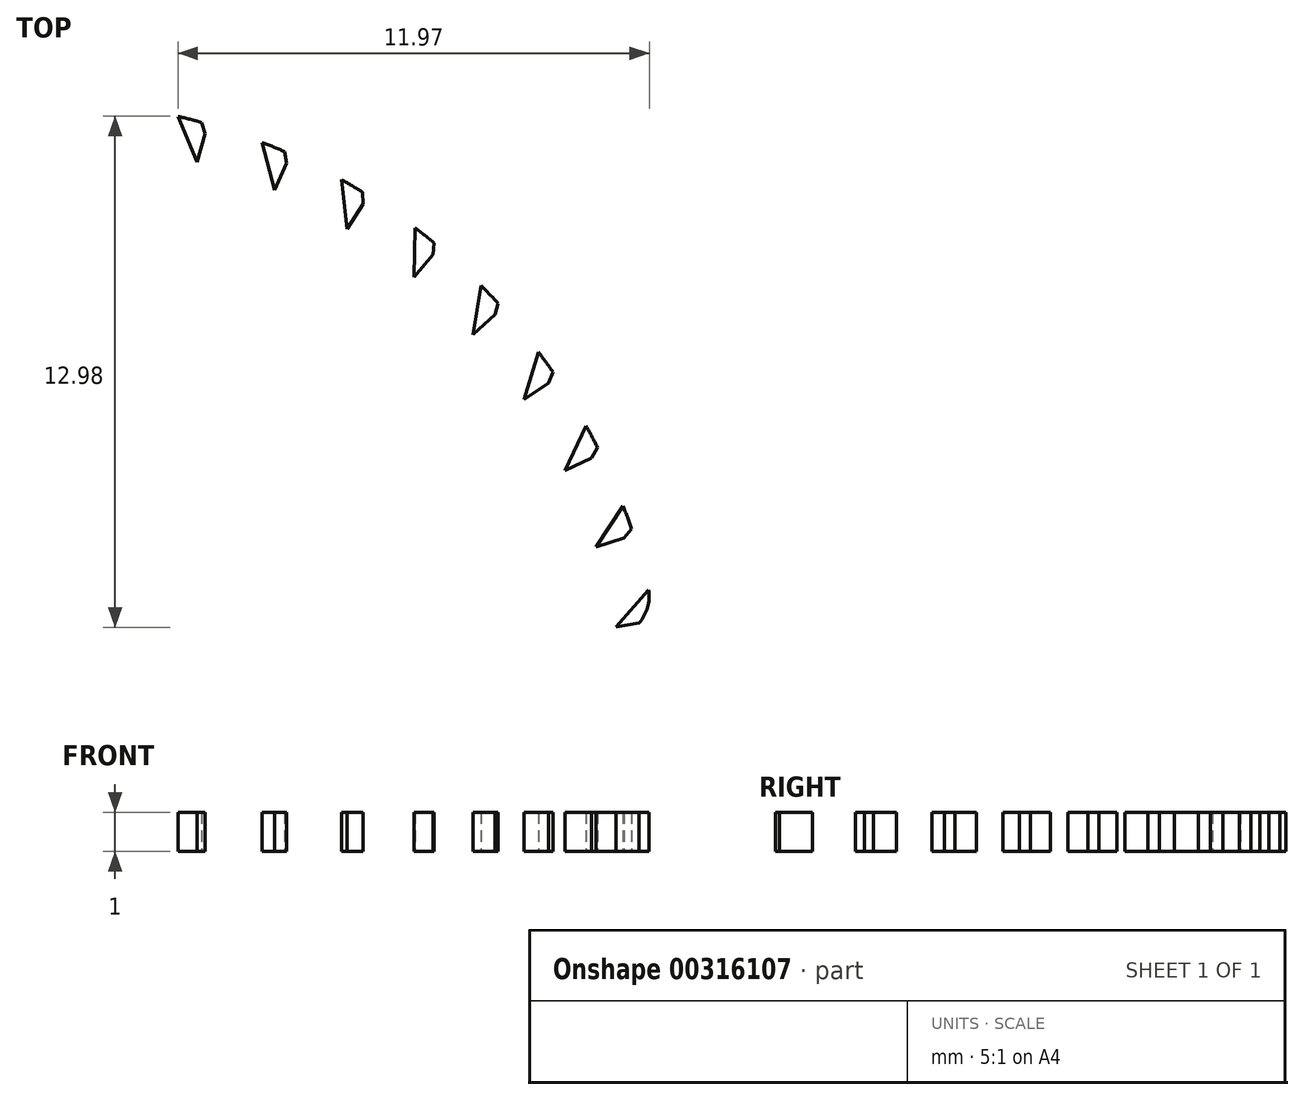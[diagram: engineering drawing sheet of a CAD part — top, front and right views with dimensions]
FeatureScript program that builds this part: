
annotation { "Feature Type Name" : "Feature", "Feature Type Description" : "" }
export const myFeature = defineFeature(function(context is Context, id is Id, definition is map)
    precondition{}
    {
        {
            var Q0;
            Q0=qCreatedBy(makeId("Top.planeOp"),FACE);
            var sketch = newSketch(context, id + "F0", { "sketchPlane" : qUnion([Q0])});
            skCircle(sketch, "E0", {"center": v(0, 0) * mm, "radius": 22.5 * mm});
            skArc(sketch, "E1", {"start": v(-10.06, -3) * mm, "mid": v(-7.42, -7.42) * mm, "end": v(-3, -10.06) * mm});
            skArc(sketch, "E2", {"start": v(-15.72, -3) * mm, "mid": v(-11.31, -11.31) * mm, "end": v(-3, -15.72) * mm});
            skArc(sketch, "E3", {"start": v(-15.72, 3) * mm, "mid": v(-12.89, 1.83) * mm, "end": v(-10.06, 3) * mm});
            skArc(sketch, "E4", {"start": v(-3, 10.06) * mm, "mid": v(-1.83, 12.89) * mm, "end": v(-3, 15.72) * mm});
            skArc(sketch, "E5.MirrorCS", {"start": v(3, 10.06) * mm, "mid": v(1.83, 12.89) * mm, "end": v(3, 15.72) * mm});
            skArc(sketch, "E6.MirrorCS", {"start": v(15.72, 3) * mm, "mid": v(12.89, 1.83) * mm, "end": v(10.06, 3) * mm});
            skArc(sketch, "E7.MirrorCS", {"start": v(15.72, -3) * mm, "mid": v(12.89, -1.83) * mm, "end": v(10.06, -3) * mm});
            skArc(sketch, "E8.MirrorCS", {"start": v(-15.72, -3) * mm, "mid": v(-12.89, -1.83) * mm, "end": v(-10.06, -3) * mm});
            skArc(sketch, "E9.MirrorCS", {"start": v(3, -10.06) * mm, "mid": v(1.83, -12.89) * mm, "end": v(3, -15.72) * mm});
            skArc(sketch, "E10.MirrorCS", {"start": v(-3, -10.06) * mm, "mid": v(-1.83, -12.89) * mm, "end": v(-3, -15.72) * mm});
            skArc(sketch, "E11.trimOffspring", {"start": v(15.72, 3) * mm, "mid": v(11.31, 11.31) * mm, "end": v(3, 15.72) * mm});
            skArc(sketch, "E12.trimOffspring", {"start": v(10.06, 3) * mm, "mid": v(7.42, 7.42) * mm, "end": v(3, 10.06) * mm});
            skArc(sketch, "E13.trimOffspring", {"start": v(-3, 15.72) * mm, "mid": v(-11.31, 11.31) * mm, "end": v(-15.72, 3) * mm});
            skArc(sketch, "E14.trimOffspring", {"start": v(-3, 10.06) * mm, "mid": v(-7.42, 7.42) * mm, "end": v(-10.06, 3) * mm});
            skArc(sketch, "E15.trimOffspring", {"start": v(3, -15.72) * mm, "mid": v(11.31, -11.31) * mm, "end": v(15.72, -3) * mm});
            skArc(sketch, "E16.trimOffspring", {"start": v(3, -10.06) * mm, "mid": v(7.42, -7.42) * mm, "end": v(10.06, -3) * mm});
            skSolve(sketch);
        }
        {
            var Q0;
            Q0=makeQuery(id+"F0.imprint","IMPRINT",FACE,{"disambiguationData":[TD([[makeQuery(id+"F0.imprint","IMPRINT",EDGE,{"derivedFrom":sQuery(id+"F0.wireOp",EDGE,"E0")}),1.0]])]});
            var Q1;
            Q1=makeQuery(id+"F0.imprint","IMPRINT",FACE,{"disambiguationData":[TD([[makeQuery(id+"F0.imprint","IMPRINT",EDGE,{"derivedFrom":sQuery(id+"F0.wireOp",EDGE,"yNKyv4sg-wyQE-NhEz-oTtB-tZKvcD1dUsbQ")}),-1.0]])]});
            var Q2;
            Q2=makeQuery(id+"F0.imprint","IMPRINT",FACE,{"disambiguationData":[TD([[makeQuery(id+"F0.imprint","IMPRINT",EDGE,{"derivedFrom":sQuery(id+"F0.wireOp",EDGE,"yNKyv4sg-wyQE-NhEz-oTtB-tZKvcD1dUsbQ")}),1.0]])]});
            var Q3;
            Q3=makeQuery(id+"F0.imprint","IMPRINT",FACE,{"disambiguationData":[TD([[makeQuery(id+"F0.imprint","IMPRINT",EDGE,{"derivedFrom":sQuery(id+"F0.wireOp",EDGE,"CHxK3Vhj-uEMq-LAEf-dkPe-Tb3R7R4YZVSK")}),1.0]])]});
            var Q4;
            Q4=makeQuery(id+"F0.imprint","IMPRINT",FACE,{"disambiguationData":[TD([[makeQuery(id+"F0.imprint","IMPRINT",EDGE,{"derivedFrom":sQuery(id+"F0.wireOp",EDGE,"CHxK3Vhj-uEMq-LAEf-dkPe-Tb3R7R4YZVSK")}),-1.0]])]});
            var Q5;
            Q5=makeQuery(id+"F0.imprint","IMPRINT",FACE,{"disambiguationData":[TD([[makeQuery(id+"F0.imprint","IMPRINT",EDGE,{"derivedFrom":sQuery(id+"F0.wireOp",EDGE,"0104c6db-07ef-44e6-b93f-2bb78c67a1090.MirrorCS")}),-1.0]])]});
            var Q6;
            Q6=makeQuery(id+"F0.imprint","IMPRINT",FACE,{"disambiguationData":[TD([[makeQuery(id+"F0.imprint","IMPRINT",EDGE,{"derivedFrom":sQuery(id+"F0.wireOp",EDGE,"0104c6db-07ef-44e6-b93f-2bb78c67a1090.MirrorCS")}),1.0]])]});
            var Q7;
            Q7=makeQuery(id+"F0.imprint","IMPRINT",FACE,{"disambiguationData":[TD([[makeQuery(id+"F0.imprint","IMPRINT",EDGE,{"derivedFrom":sQuery(id+"F0.wireOp",EDGE,"970dafef-14e2-4ce6-b4dc-0c507e57a7b30.MirrorCS")}),-1.0]])]});
            var Q8;
            Q8=makeQuery(id+"F0.imprint","IMPRINT",FACE,{"disambiguationData":[TD([[makeQuery(id+"F0.imprint","IMPRINT",EDGE,{"derivedFrom":sQuery(id+"F0.wireOp",EDGE,"93014a0a-df88-4f59-a375-decd953fd38a0.MirrorCS")}),1.0]])]});
            var Q9;
            Q9=makeQuery(id+"F0.imprint","IMPRINT",FACE,{"disambiguationData":[TD([[makeQuery(id+"F0.imprint","IMPRINT",EDGE,{"derivedFrom":sQuery(id+"F0.wireOp",EDGE,"3d9ed699-9ae5-43d2-bffb-ac21203e5f350.MirrorCS")}),-1.0]])]});
            var Q10;
            Q10=makeQuery(id+"F0.imprint","IMPRINT",FACE,{"disambiguationData":[TD([[makeQuery(id+"F0.imprint","IMPRINT",EDGE,{"derivedFrom":sQuery(id+"F0.wireOp",EDGE,"3d9ed699-9ae5-43d2-bffb-ac21203e5f350.MirrorCS")}),1.0]])]});
            var Q11;
            Q11=makeQuery(id+"F0.imprint","IMPRINT",FACE,{"disambiguationData":[TD([[makeQuery(id+"F0.imprint","IMPRINT",EDGE,{"derivedFrom":sQuery(id+"F0.wireOp",EDGE,"e82f33f2-ffd0-4327-8124-6c5fd45a99620.MirrorCS")}),-1.0]])]});
            var Q12;
            Q12=makeQuery(id+"F0.imprint","IMPRINT",FACE,{"disambiguationData":[TD([[makeQuery(id+"F0.imprint","IMPRINT",EDGE,{"derivedFrom":sQuery(id+"F0.wireOp",EDGE,"cda73c98-9fc0-4e18-aa02-a1f205a2015f0.MirrorCS")}),-1.0]])]});
            var Q13;
            {var subQ4=sQuery(id+"F0.wireOp",EDGE,"64d5d3fe-6fde-471c-9a08-4dfe694e491e0.MirrorCS");Q13=makeQuery(id+"F0.imprint","IMPRINT",FACE,{"disambiguationData":[TD([[makeQuery(id+"F0.imprint","IMPRINT",EDGE,{"derivedFrom":subQ4}),-1.0]])]});}
            var Q14;
            {var subQ1=sQuery(id+"F0.wireOp",EDGE,"64d5d3fe-6fde-471c-9a08-4dfe694e491e0.MirrorCS");Q14=makeQuery(id+"F0.imprint","IMPRINT",FACE,{"disambiguationData":[TD([[makeQuery(id+"F0.imprint","IMPRINT",EDGE,{"derivedFrom":subQ1}),1.0]])]});}
            var Q15;
            {var subQ4=sQuery(id+"F0.wireOp",EDGE,"3d1d17da-de2a-4a28-b4d7-ecdb04be73e10.MirrorCS");Q15=makeQuery(id+"F0.imprint","IMPRINT",FACE,{"disambiguationData":[TD([[makeQuery(id+"F0.imprint","IMPRINT",EDGE,{"derivedFrom":subQ4}),-1.0]])]});}
            var Q16;
            {var subQ0=sQuery(id+"F0.wireOp",EDGE,"ec8af088-ad77-4baf-9b99-9a8c1ec1802f0.MirrorCS");var subQ1=sQuery(id+"F0.wireOp",EDGE,"qaeiCQc8-Z452-aFcL-8diV-bsPXyrLEfwMX");var subQ2=makeQuery(id+"F0.imprint","INTERSECT",VERTEX,{"disambiguationData":[OD(0.0)],"derivedFrom":[subQ1,subQ0]});Q16=makeQuery(id+"F0.imprint","IMPRINT",FACE,{"disambiguationData":[TD([[makeQuery(id+"F0.imprint","IMPRINT",EDGE,{"disambiguationData":[TD([[subQ2,-1.0]])],"derivedFrom":subQ1}),-1.0]])]});}
            var Q17;
            {var subQ1=sQuery(id+"F0.wireOp",EDGE,"3a8932c2-975d-4770-829d-42bc38e53c8a0.MirrorCS");var subQ3=sQuery(id+"F0.wireOp",EDGE,"9286b3fb-68f5-4dff-b94a-b65767a80ac30.MirrorCS");var subQ5=makeQuery(id+"F0.imprint","INTERSECT",VERTEX,{"disambiguationData":[OD(0.0)],"derivedFrom":[subQ1,subQ3]});Q17=makeQuery(id+"F0.imprint","IMPRINT",FACE,{"disambiguationData":[TD([[makeQuery(id+"F0.imprint","IMPRINT",EDGE,{"disambiguationData":[TD([[subQ5,-1.0]])],"derivedFrom":subQ1}),-1.0]])]});}
            var Q18;
            {var subQ0=sQuery(id+"F0.wireOp",EDGE,"768f1834-c769-483f-ae03-996157da35af0.MirrorCS");var subQ1=sQuery(id+"F0.wireOp",EDGE,"3a8932c2-975d-4770-829d-42bc38e53c8a0.MirrorCS");var subQ2=makeQuery(id+"F0.imprint","INTERSECT",VERTEX,{"disambiguationData":[OD(0.0)],"derivedFrom":[subQ1,subQ0]});Q18=makeQuery(id+"F0.imprint","IMPRINT",FACE,{"disambiguationData":[TD([[makeQuery(id+"F0.imprint","IMPRINT",EDGE,{"disambiguationData":[TD([[subQ2,-1.0]])],"derivedFrom":subQ1}),-1.0]])]});}
            var Q19;
            {var subQ0=sQuery(id+"F0.wireOp",EDGE,"fbead855-19f8-497d-95b7-98c132a5b90d0.MirrorCS");var subQ1=sQuery(id+"F0.wireOp",EDGE,"QfTjW5H5-HH3x-KSd2-ifWf-9xdCikRYGM0G");var subQ2=makeQuery(id+"F0.imprint","INTERSECT",VERTEX,{"disambiguationData":[OD(0.0)],"derivedFrom":[subQ1,subQ0]});Q19=makeQuery(id+"F0.imprint","IMPRINT",FACE,{"disambiguationData":[TD([[makeQuery(id+"F0.imprint","IMPRINT",EDGE,{"disambiguationData":[TD([[subQ2,-1.0]])],"derivedFrom":subQ1}),1.0]])]});}
            var Q20;
            {var subQ7=sQuery(id+"F0.wireOp",EDGE,"b429edeb-7c72-4fef-b483-5a4b1cd2d26d0.MirrorCS");Q20=makeQuery(id+"F0.imprint","IMPRINT",FACE,{"disambiguationData":[TD([[makeQuery(id+"F0.imprint","IMPRINT",EDGE,{"derivedFrom":subQ7}),-1.0]])]});}
            var Q21;
            {var subQ0=sQuery(id+"F0.wireOp",EDGE,"ec8af088-ad77-4baf-9b99-9a8c1ec1802f0.MirrorCS");var subQ1=sQuery(id+"F0.wireOp",EDGE,"qaeiCQc8-Z452-aFcL-8diV-bsPXyrLEfwMX");var subQ2=makeQuery(id+"F0.imprint","INTERSECT",VERTEX,{"disambiguationData":[OD(0.0)],"derivedFrom":[subQ1,subQ0]});Q21=makeQuery(id+"F0.imprint","IMPRINT",FACE,{"disambiguationData":[TD([[makeQuery(id+"F0.imprint","IMPRINT",EDGE,{"disambiguationData":[TD([[subQ2,-1.0]])],"derivedFrom":subQ1}),1.0]])]});}
            var Q22;
            {var subQ0=sQuery(id+"F0.wireOp",EDGE,"9286b3fb-68f5-4dff-b94a-b65767a80ac30.MirrorCS");var subQ1=sQuery(id+"F0.wireOp",EDGE,"57974e39-1009-42e2-ba5a-03edd4ff50a40.MirrorCS");var subQ2=makeQuery(id+"F0.imprint","INTERSECT",VERTEX,{"disambiguationData":[OD(0.0)],"derivedFrom":[subQ1,subQ0]});Q22=makeQuery(id+"F0.imprint","IMPRINT",FACE,{"disambiguationData":[TD([[makeQuery(id+"F0.imprint","IMPRINT",EDGE,{"disambiguationData":[TD([[subQ2,-1.0]])],"derivedFrom":subQ1}),-1.0]])]});}
            var Q23;
            Q23=makeQuery(id+"F0.imprint","IMPRINT",FACE,{"disambiguationData":[TD([[makeQuery(id+"F0.imprint","IMPRINT",EDGE,{"derivedFrom":sQuery(id+"F0.wireOp",EDGE,"E5.MirrorCS")}),-1.0]])]});
            var Q24;
            Q24=makeQuery(id+"F0.imprint","IMPRINT",FACE,{"disambiguationData":[TD([[makeQuery(id+"F0.imprint","IMPRINT",EDGE,{"derivedFrom":sQuery(id+"F0.wireOp",EDGE,"E3")}),1.0]])]});
            var Q25;
            Q25=makeQuery(id+"F0.imprint","IMPRINT",FACE,{"disambiguationData":[TD([[makeQuery(id+"F0.imprint","IMPRINT",EDGE,{"derivedFrom":sQuery(id+"F0.wireOp",EDGE,"E1")}),-1.0]])]});
            var Q26;
            Q26=makeQuery(id+"F0.imprint","IMPRINT",FACE,{"disambiguationData":[TD([[makeQuery(id+"F0.imprint","IMPRINT",EDGE,{"derivedFrom":sQuery(id+"F0.wireOp",EDGE,"E7.MirrorCS")}),1.0]])]});
            extrude(context, id + "F1", {"entities" : qUnion([Q0, Q1, Q2, Q3, Q4, Q5, Q6, Q7, Q8, Q9, Q10, Q11, Q12, Q13, Q14, Q15, Q16, Q17, Q18, Q19, Q20, Q21, Q22, Q23, Q24, Q25, Q26]), "depth" : 4 * mm});
        }
        {
            var Q0;
            Q0=makeQuery(id+"F1.opExtrude","CAP_FACE",FACE,{"disambiguationData":[OSD([sQuery(id+"F0.wireOp",EDGE,"E0"),sQuery(id+"F0.wireOp",EDGE,"yNKyv4sg-wyQE-NhEz-oTtB-tZKvcD1dUsbQ")])],"isStart":false});
            var sketch = newSketch(context, id + "F2", { "sketchPlane" : qUnion([Q0])});
            skPoint(sketch, "E17.middle", {"position": v(0, 15) * mm});
            skLineSegment(sketch, "E18", {"start": v(0, 15) * mm, "end": v(0, 15.75) * mm});
            skLineSegment(sketch, "E19", {"start": v(0, 22.5) * mm, "end": v(0, 21.5) * mm});
            skLineSegment(sketch, "E20.MirrorCS", {"start": v(0, 21.5) * mm, "end": v(-2, 18.75) * mm});
            skLineSegment(sketch, "E21.MirrorCS", {"start": v(-2, 18.75) * mm, "end": v(0, 15.75) * mm});
            skLineSegment(sketch, "E22.MirrorCS", {"start": v(-3, 18.75) * mm, "end": v(0, 15) * mm});
            skLineSegment(sketch, "E23.MirrorCS", {"start": v(0, 22.5) * mm, "end": v(-3, 18.75) * mm});
            skSolve(sketch);
        }
        {
            var Q0;
            Q0=makeQuery(id+"F2.imprint","IMPRINT",FACE,{"disambiguationData":[TD([[makeQuery(id+"F2.imprint","IMPRINT",EDGE,{"derivedFrom":sQuery(id+"F2.wireOp",EDGE,"E18")}),1.0]])]});
            extrude(context, id + "F3", {"entities" : qUnion([Q0]), "depth" : 1 * mm});
        }
        {
            var Q0;
            Q0=makeQuery(id+"F3.opExtrude","SWEPT_BODY",BODY,{"disambiguationData":[OSD([sQuery(id+"F2.wireOp",EDGE,"E18"),sQuery(id+"F2.wireOp",EDGE,"E19"),sQuery(id+"F2.wireOp",EDGE,"E20.MirrorCS"),sQuery(id+"F2.wireOp",EDGE,"E21.MirrorCS"),sQuery(id+"F2.wireOp",EDGE,"E22.MirrorCS"),sQuery(id+"F2.wireOp",EDGE,"E23.MirrorCS")])]});
            var Q1;
            Q1=sQuery(id+"F0.wireOp",EDGE,"E0");
            circularPattern(context, id + "F4", {"operationType" : NewBodyOperationType.ADD, "entities" : qUnion([Q0]), "axis" : qUnion([Q1]), "angle" : 360 * degree, "instanceCount" : 45, "equalSpace" : true});
        }
        {
            var Q0;
            Q0=makeQuery(id+"F0.imprint","IMPRINT",FACE,{"disambiguationData":[TD([[makeQuery(id+"F0.imprint","IMPRINT",EDGE,{"derivedFrom":sQuery(id+"F0.wireOp",EDGE,"E3")}),1.0]])]});
            var Q1;
            Q1=makeQuery(id+"F0.imprint","IMPRINT",FACE,{"disambiguationData":[TD([[makeQuery(id+"F0.imprint","IMPRINT",EDGE,{"derivedFrom":sQuery(id+"F0.wireOp",EDGE,"E7.MirrorCS")}),1.0]])]});
            var Q2;
            Q2=makeQuery(id+"F0.imprint","IMPRINT",FACE,{"disambiguationData":[TD([[makeQuery(id+"F0.imprint","IMPRINT",EDGE,{"derivedFrom":sQuery(id+"F0.wireOp",EDGE,"E5.MirrorCS")}),-1.0]])]});
            var Q3;
            Q3=makeQuery(id+"F0.imprint","IMPRINT",FACE,{"disambiguationData":[TD([[makeQuery(id+"F0.imprint","IMPRINT",EDGE,{"derivedFrom":sQuery(id+"F0.wireOp",EDGE,"E1")}),-1.0]])]});
            extrude(context, id + "F5", {"entities" : qUnion([Q0, Q1, Q2, Q3]), "operationType" : NewBodyOperationType.REMOVE, "depth" : 25 * mm});
        }
        {
            var Q0;
            Q0=makeQuery(id+"F0.imprint","IMPRINT",FACE,{"disambiguationData":[TD([[makeQuery(id+"F0.imprint","IMPRINT",EDGE,{"derivedFrom":sQuery(id+"F0.wireOp",EDGE,"E0")}),1.0]])]});
            var sketch = newSketch(context, id + "F6", { "sketchPlane" : qUnion([Q0])});
            skCircle(sketch, "E24", {"center": v(0, 0) * mm, "radius": 18.5 * mm});
            skCircle(sketch, "E25", {"center": v(0, 0) * mm, "radius": 8 * mm});
            skSolve(sketch);
        }
        {
            var Q0;
            Q0=makeQuery(id+"F3yU1fKuAJjoYRn_1.boolean.opBoolean","COPY",EDGE,{"derivedFrom":makeQuery(id+"F3yU1fKuAJjoYRn_1.opExtrude","CAP_EDGE",EDGE,{"disambiguationData":[OSD([sQuery(id+"F6.wireOp",EDGE,"E25")])],"isStart":true})});
            var Q1;
            Q1=makeQuery(id+"F3yU1fKuAJjoYRn_1.boolean.opBoolean","COPY",EDGE,{"derivedFrom":makeQuery(id+"F3yU1fKuAJjoYRn_1.opExtrude","CAP_EDGE",EDGE,{"disambiguationData":[OSD([sQuery(id+"F6.wireOp",EDGE,"E24")])],"isStart":true})});
            var Q2;
            Q2=makeQuery(id+"F3yU1fKuAJjoYRn_1.boolean.opBoolean","COPY",EDGE,{"derivedFrom":makeQuery(id+"F3yU1fKuAJjoYRn_1.opExtrude","CAP_EDGE",EDGE,{"disambiguationData":[OSD([sQuery(id+"F6.wireOp",EDGE,"E25")])],"isStart":false})});
            var Q3;
            Q3=makeQuery(id+"F3yU1fKuAJjoYRn_1.boolean.opBoolean","COPY",EDGE,{"derivedFrom":makeQuery(id+"F3yU1fKuAJjoYRn_1.opExtrude","CAP_EDGE",EDGE,{"disambiguationData":[OSD([sQuery(id+"F6.wireOp",EDGE,"E24")])],"isStart":false})});
            var Q4;
            Q4=makeQuery(id+"F5.boolean.opBoolean","COPY",EDGE,{"derivedFrom":makeQuery(id+"F5.opExtrude","SWEPT_EDGE",EDGE,{"disambiguationData":[OSD([sQuery(id+"F0.wireOp",EDGE,"E2"),sQuery(id+"F0.wireOp",EDGE,"E8.MirrorCS")])]})});
            var Q5;
            Q5=makeQuery(id+"F5.boolean.opBoolean","COPY",EDGE,{"derivedFrom":makeQuery(id+"F5.opExtrude","SWEPT_EDGE",EDGE,{"disambiguationData":[OSD([sQuery(id+"F0.wireOp",EDGE,"E2"),sQuery(id+"F0.wireOp",EDGE,"E10.MirrorCS")])]})});
            var Q6;
            Q6=makeQuery(id+"F5.boolean.opBoolean","COPY",EDGE,{"derivedFrom":makeQuery(id+"F5.opExtrude","SWEPT_EDGE",EDGE,{"disambiguationData":[OSD([sQuery(id+"F0.wireOp",EDGE,"E9.MirrorCS"),sQuery(id+"F0.wireOp",EDGE,"E15.trimOffspring")])]})});
            var Q7;
            Q7=makeQuery(id+"F5.boolean.opBoolean","COPY",EDGE,{"derivedFrom":makeQuery(id+"F5.opExtrude","SWEPT_EDGE",EDGE,{"disambiguationData":[OSD([sQuery(id+"F0.wireOp",EDGE,"E6.MirrorCS"),sQuery(id+"F0.wireOp",EDGE,"E11.trimOffspring")])]})});
            var Q8;
            Q8=makeQuery(id+"F5.boolean.opBoolean","COPY",EDGE,{"derivedFrom":makeQuery(id+"F5.opExtrude","SWEPT_EDGE",EDGE,{"disambiguationData":[OSD([sQuery(id+"F0.wireOp",EDGE,"E7.MirrorCS"),sQuery(id+"F0.wireOp",EDGE,"E15.trimOffspring")])]})});
            var Q9;
            Q9=makeQuery(id+"F5.boolean.opBoolean","COPY",EDGE,{"derivedFrom":makeQuery(id+"F5.opExtrude","SWEPT_EDGE",EDGE,{"disambiguationData":[OSD([sQuery(id+"F0.wireOp",EDGE,"E3"),sQuery(id+"F0.wireOp",EDGE,"E13.trimOffspring")])]})});
            var Q10;
            Q10=makeQuery(id+"F5.boolean.opBoolean","COPY",EDGE,{"derivedFrom":makeQuery(id+"F5.opExtrude","SWEPT_EDGE",EDGE,{"disambiguationData":[OSD([sQuery(id+"F0.wireOp",EDGE,"E5.MirrorCS"),sQuery(id+"F0.wireOp",EDGE,"E11.trimOffspring")])]})});
            var Q11;
            Q11=makeQuery(id+"F5.boolean.opBoolean","COPY",EDGE,{"derivedFrom":makeQuery(id+"F5.opExtrude","SWEPT_EDGE",EDGE,{"disambiguationData":[OSD([sQuery(id+"F0.wireOp",EDGE,"E4"),sQuery(id+"F0.wireOp",EDGE,"E13.trimOffspring")])]})});
            var Q12;
            Q12=makeQuery(id+"F1.opExtrude","CAP_EDGE",EDGE,{"disambiguationData":[OSD([sQuery(id+"F0.wireOp",EDGE,"E0")])],"isStart":true});
            var Q13;
            Q13=makeQuery(id+"F1.opExtrude","SWEPT_FACE",FACE,{"disambiguationData":[OSD([sQuery(id+"F0.wireOp",EDGE,"E0")])]});
            fillet(context, id + "F7", {"entities" : qUnion([Q0, Q1, Q2, Q3, Q4, Q5, Q6, Q7, Q8, Q9, Q10, Q11, Q12, Q13]), "radius" : 1 * mm, "tangentPropagation" : true, "allowEdgeOverflow" : false});
        }
    });
